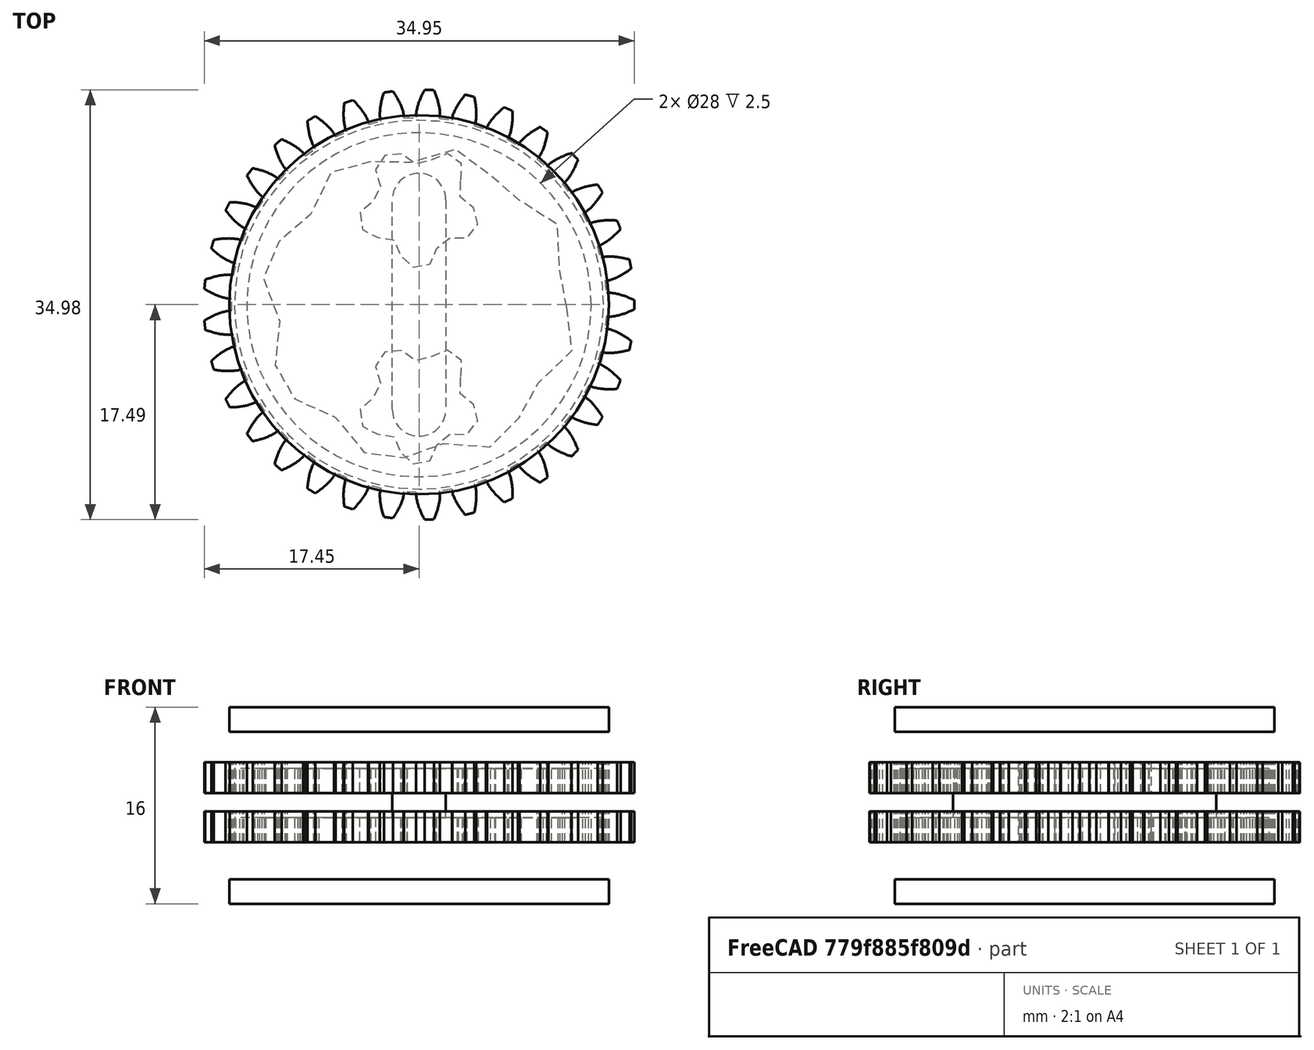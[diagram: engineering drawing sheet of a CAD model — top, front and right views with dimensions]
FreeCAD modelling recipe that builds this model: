
FCSTD DOCUMENT  (FreeCAD 0.16RUnknown)
Label: PlanetaryDifferential
License: CreativeCommons Attribution-NonCommercial
LicenseURL: http://creativecommons.org/licenses/by-nc/4.0/
objects: PartDesign::Pad×6, Sketcher::SketchObject×4, Part::Part2DObjectPython×4, Part::Feature×4, Mesh::Feature×2, Part::Cut×2, Part::FeaturePython×1
note: 27 computed .brp shape members not serialized (recipe doc carries the construction recipe); baked Part::Feature solids carry a one-line shape summary decoded from their .brp

FEATURE [Sketcher::SketchObject] Sketch
  sketch-geometry (2):
    g0: Circle CenterX=0 CenterY=0 CenterZ=0 NormalX=0 NormalY=0 NormalZ=1 Radius=15
    g1: Circle [constr] CenterX=0 CenterY=0 CenterZ=0 NormalX=0 NormalY=0 NormalZ=1 Radius=3
  constraints (4):
    c: Coincident(g0,g-1)
    c: Coincident(g1,g-1)
    c: Radius(g1) = 3
    c: Radius(g0) = 15
FEATURE [Part::Part2DObjectPython] BSpline002  # Draft 2D object (typed FeaturePython)
  Closed = true
  MakeFace = true
  Points = (1000) [(8.00842,-0.199823,0),(8.02171,-0.198999,0),(8.04301,-0.196545,0),(8.0721,-0.191305,0),(8.10745,-0.182451,0),(8.14838,-0.169185,0),+994 more]
FEATURE [Mesh::Feature] Annulus
FEATURE [Mesh::Feature] Planet
FEATURE [Part::Part2DObjectPython] BSpline  # Draft 2D object (typed FeaturePython)
  Closed = true
  MakeFace = true
  Placement = pos=(0,-8,1) rot=(0,0,1;0.610865rad)
  Points = (1000) [(4.00427,-0.199954,0),(4.01092,-0.199726,0),(4.01978,-0.199159,0),(4.03119,-0.198038,0),(4.04446,-0.196244,0),(4.05944,-0.193651,0),+994 more]
FEATURE [Part::Part2DObjectPython] BSpline003  # Draft 2D object (typed FeaturePython)
  Closed = true
  MakeFace = true
  Points = (1000) [(8.00842,-0.199823,0),(8.02171,-0.198999,0),(8.04301,-0.196545,0),(8.0721,-0.191305,0),(8.10745,-0.182451,0),(8.14838,-0.169185,0),+994 more]
FEATURE [Part::Part2DObjectPython] BSpline004  # Draft 2D object (typed FeaturePython)
  Closed = true
  MakeFace = true
  Points = (1000) [(12.0126,-0.199604,0),(12.034,-0.197717,0),(12.0722,-0.191375,0),(12.1256,-0.177253,0),(12.1912,-0.152862,0),(12.2665,-0.115999,0),+994 more]
FEATURE [PartDesign::Pad] Pad
  Length = 2
  Length2 = 100
  Sketch = -> Sketch
  Type = 0
FEATURE [PartDesign::Pad] Pad001
  Length = 2
  Length2 = 100
  Sketch = -> BSpline004
  Type = 0
FEATURE [Part::Cut] Cut
  Base = -> Pad
  Placement = pos=(0,0,-3) rot=(0,0,1;0rad)
  Tool = -> Pad001
FEATURE [PartDesign::Pad] Pad002
  Length = 2
  Length2 = 100
  Placement = pos=(0,-8,1) rot=(0,0,1;0.610865rad)
  Sketch = -> BSpline
  Type = 0
FEATURE [Sketcher::SketchObject] Sketch001
  Support = -> BSpline002 [Face1]
  sketch-geometry (6):
    g0: ArcOfCircle CenterX=0 CenterY=8.53055 CenterZ=0 NormalX=0 NormalY=0 NormalZ=1 Radius=2.16804 StartAngle=0 EndAngle=3.14159
    g1: ArcOfCircle CenterX=0 CenterY=-8.53055 CenterZ=0 NormalX=0 NormalY=0 NormalZ=1 Radius=2.16804 StartAngle=3.14159 EndAngle=6.28319
    g2: LineSegment [constr] StartX=-2.16804 StartY=8.53055 StartZ=0 EndX=2.16804 EndY=8.53055 EndZ=0
    g3: LineSegment StartX=2.16804 StartY=8.53055 StartZ=0 EndX=2.16804 EndY=-8.53055 EndZ=0
    g4: LineSegment [constr] StartX=2.16804 StartY=-8.53055 StartZ=0 EndX=-2.16804 EndY=-8.53055 EndZ=0
    g5: LineSegment StartX=-2.16804 StartY=-8.53055 StartZ=0 EndX=-2.16804 EndY=8.53055 EndZ=0
  constraints (16):
    c: PointOnObject(g0,g-2)
    c: PointOnObject(g1,g-2)
    c: Coincident(g2,g3)
    c: Coincident(g3,g4)
    c: Coincident(g4,g5)
    c: Coincident(g5,g2)
    c: Horizontal(g2)
    c: Horizontal(g4)
    c: Vertical(g5)
    c: Coincident(g0,g2)
    c: Coincident(g0,g2)
    c: Coincident(g1,g4)
    c: Coincident(g1,g3)
    c: PointOnObject(g0,g2)
    c: PointOnObject(g1,g4)
    c: Symmetric(g1,g0,g-1)
FEATURE [Part::FeaturePython] InvoluteGear  # WARN: FeaturePython — macro-defined, semantics opaque (R4)
  backlash = 0
  beta = 0
  clearance = 0.25
  height = 2.5
  module = 1
  numpoints = 6
  pressure_angle = 20
  shift = 0
  simple = false
  teeth = 33
  undercut = false
FEATURE [PartDesign::Pad] Pad003
  Length = 2
  Length2 = 100
  Midplane = true
  Reversed = true
  Sketch = -> Sketch001
  Type = 0
FEATURE [Sketcher::SketchObject] Sketch002
  sketch-geometry (1):
    g0: Circle CenterX=0 CenterY=0 CenterZ=0 NormalX=0 NormalY=0 NormalZ=1 Radius=14
  constraints (2):
    c: Coincident(g0,g-1)
    c: Radius(g0) = 14
FEATURE [PartDesign::Pad] Pad004
  Length = 10
  Length2 = 100
  Midplane = true
  Sketch = -> Sketch002
  Type = 0
FEATURE [Part::Cut] Cut001
  Base = -> InvoluteGear
  Placement = pos=(0,0,1) rot=(0,0,1;0rad)
  Tool = -> Pad004
FEATURE [Part::Feature] Pad002001  label="Pad002"
  Placement = pos=(0,8,-3) rot=(0,0,1;0.610865rad)
  shape: bbox 9.673 x 9.391 x 2 mm, 3 faces (baked)
FEATURE [Part::Feature] Cut001001  label="Cut001"
  Placement = pos=(0,0,-3) rot=(0,0,1;0rad)
  shape: bbox 34.95 x 34.99 x 2.5 mm, 201 faces (baked)
FEATURE [Part::Feature] Cut001002  label="Cut"
  Placement = pos=(0,0,1) rot=(0,0,1;0rad)
  shape: bbox 30 x 30 x 2 mm, 4 faces (baked)
FEATURE [Sketcher::SketchObject] Sketch003
  Placement = pos=(0,0,6) rot=(0,0,1;0rad)
  sketch-geometry (1):
    g0: Circle CenterX=0 CenterY=0 CenterZ=0 NormalX=0 NormalY=0 NormalZ=1 Radius=15.4296
  constraints (1):
    c: Coincident(g0,g-1)
FEATURE [PartDesign::Pad] Pad002002
  Length = 2
  Length2 = 100
  Placement = pos=(0,0,6) rot=(0,0,1;0rad)
  Sketch = -> Sketch003
  Type = 0
FEATURE [Part::Feature] Pad002002001  label="Pad002002"
  Placement = pos=(0,0,-8) rot=(0,0,1;0rad)
  shape: bbox 30.86 x 30.86 x 2 mm, 3 faces (baked)
